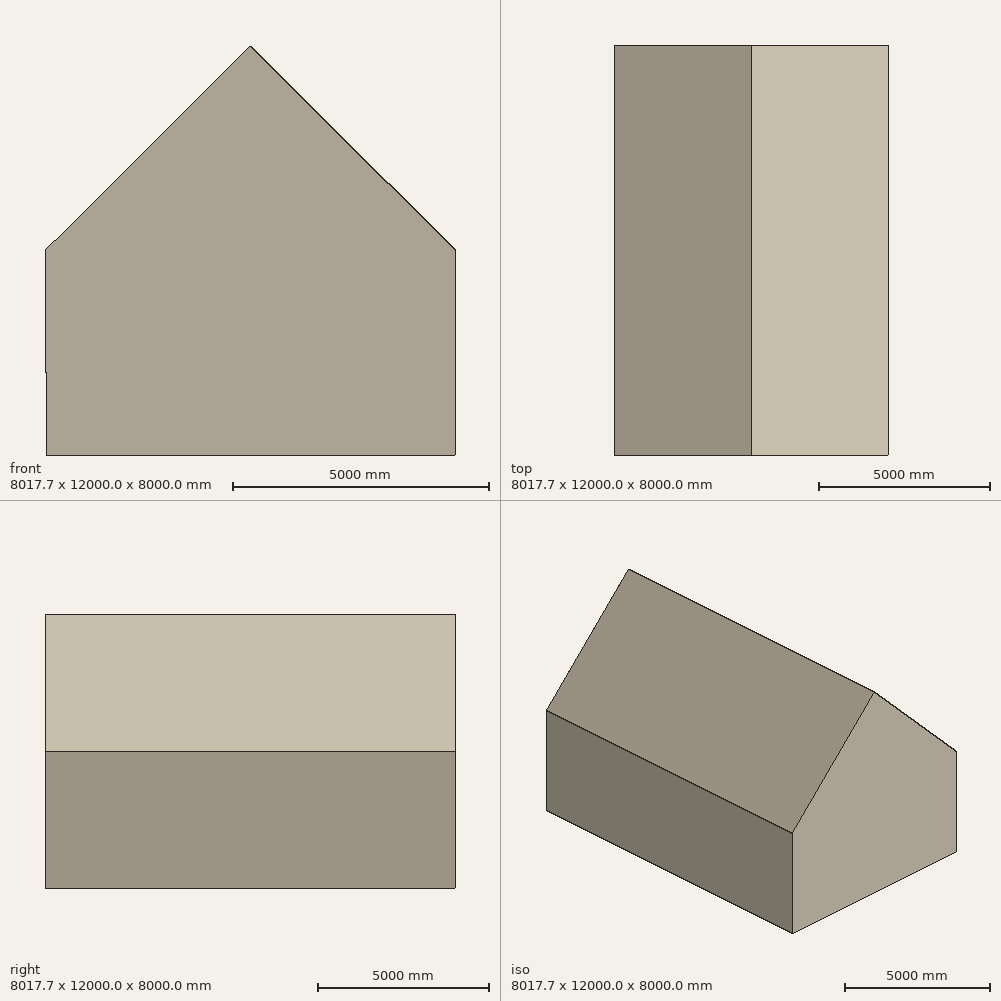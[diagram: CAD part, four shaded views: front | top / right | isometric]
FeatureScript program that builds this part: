
annotation { "Feature Type Name" : "Feature", "Feature Type Description" : "" }
export const myFeature = defineFeature(function(context is Context, id is Id, definition is map)
    precondition{}
    {
        {
            var Q0;
            Q0=qCreatedBy(makeId("Front.planeOp"),FACE);
            var sketch = newSketch(context, id + "F0", { "sketchPlane" : qUnion([Q0])});
            skLineSegment(sketch, "E0", {"start": v(-3997.63, -4360.11) * mm, "end": v(4002.37, -4360.11) * mm});
            skLineSegment(sketch, "E1", {"start": v(4002.37, -4360.11) * mm, "end": v(4002.37, -360.15) * mm});
            skLineSegment(sketch, "E2", {"start": v(4002.37, -360.15) * mm, "end": v(0, 3639.85) * mm});
            skLineSegment(sketch, "E3", {"start": v(0, 3639.85) * mm, "end": v(-4015.33, -360.15) * mm});
            skLineSegment(sketch, "E4", {"start": v(-4015.33, -360.15) * mm, "end": v(-3997.63, -4360.11) * mm});
            skSolve(sketch);
        }
        {
            var Q0;
            Q0 = qSketchRegion(id + "F0", true);
            extrude(context, id + "F1", {"entities" : qUnion([Q0]), "depth" : 12000 * mm});
        }
    });
